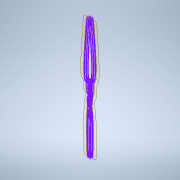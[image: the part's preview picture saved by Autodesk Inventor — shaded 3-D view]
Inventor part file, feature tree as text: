
AUTODESK INVENTOR PART (.ipt)
format: ipt  version: 2022 (Build 260153000, 153)  size: 2,741,248 bytes
history: native  units: mm
features: sketch x8, other x4, surface_op x2, sweep x2
ambient origin geometry x8: Origin, YZ Plane, XZ Plane, XY Plane, X Axis, Y Axis, Z Axis, Center Point
bodies: Body1 (feature_tree), Body2 (feature_tree), Body3 (feature_tree), Body4 (feature_tree), Body5 (feature_tree), Body6 (feature_tree), Body7 (feature_tree), Body8 (feature_tree), Body9 (feature_tree), Body10 (feature_tree), Body11 (feature_tree), Body12 (feature_tree), Body13 (feature_tree), Body14 (feature_tree), Body15 (feature_tree), Body16 (feature_tree), Body17 (feature_tree), Body18 (feature_tree), Body19 (feature_tree), Body20 (feature_tree), Body21 (feature_tree), Body22 (feature_tree), Body23 (feature_tree), Body24 (feature_tree), Body25 (feature_tree), Body26 (feature_tree), Body27 (feature_tree), Body28 (feature_tree), Body29 (feature_tree), Body30 (feature_tree), Body31 (feature_tree), Body32 (feature_tree), Body33 (feature_tree), Body34 (feature_tree)
feature tree (16):
  sketch  "Sketch1"  dims[d0=330.0mm d1=90.0deg]
  sketch  "3D Sketch3"
  sketch  "3D Sketch4"
  surface_op  "Stitch Surface1"
  sketch  "3D Sketch1"
  sketch  "Sketch2"  dims[d2=0.0mm d3=0.0mm d4=330.0mm]
  other  "Srf1"
  sketch  "3D Sketch2"
  sketch  "Sketch3"  dims[d5=90.0deg d6=0.0mm d7=0.0mm d13=0.0mm]
  other  "Srf2"
  other  "Srf4"
  sketch  "3D Sketch5"
  other  "Srf6"
  sweep  "SweepSrf1"
  sweep  "SweepSrf2"
  surface_op  "Boundary Patch3"
